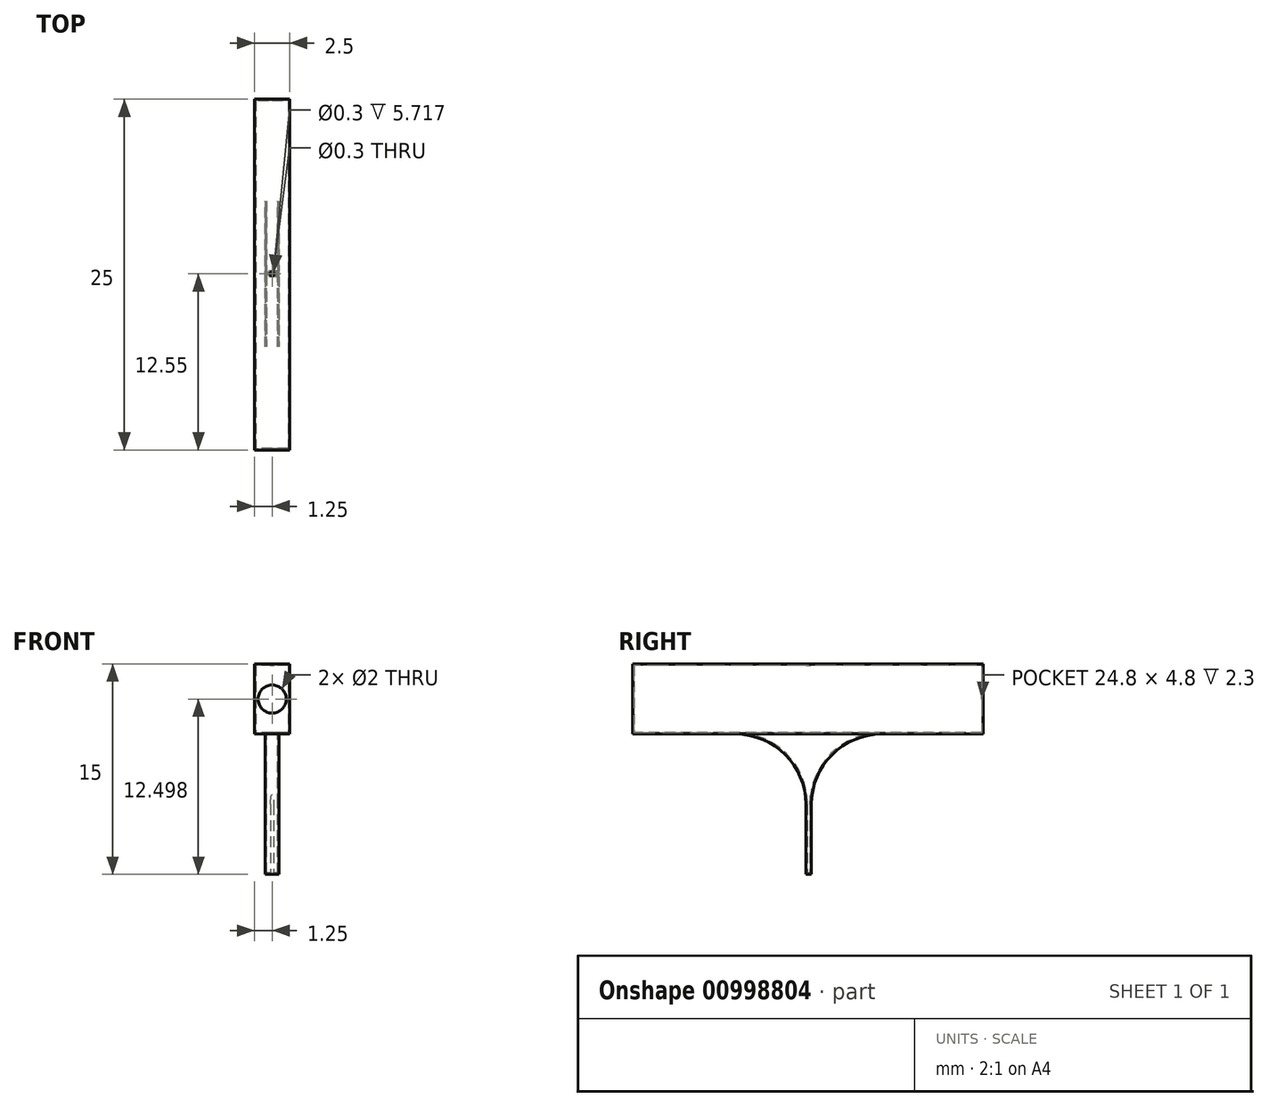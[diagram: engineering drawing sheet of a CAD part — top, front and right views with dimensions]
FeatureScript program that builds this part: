
annotation { "Feature Type Name" : "Feature", "Feature Type Description" : "" }
export const myFeature = defineFeature(function(context is Context, id is Id, definition is map)
    precondition{}
    {
        {
            var Q0;
            Q0=qCreatedBy(makeId("Right.planeOp"),FACE);
            var sketch = newSketch(context, id + "F0", { "sketchPlane" : qUnion([Q0])});
            skLineSegment(sketch, "E0.bottom", {"start": v(-96.83, 24.86) * mm, "end": v(-121.83, 24.86) * mm});
            skLineSegment(sketch, "E0.top", {"start": v(-114.33, 19.86) * mm, "end": v(-121.83, 19.86) * mm});
            skLineSegment(sketch, "E0.left", {"start": v(-96.83, 24.86) * mm, "end": v(-96.83, 19.86) * mm});
            skLineSegment(sketch, "E0.right", {"start": v(-121.83, 24.86) * mm, "end": v(-121.83, 19.86) * mm});
            skLineSegment(sketch, "E1", {"start": v(-96.78, 19.86) * mm, "end": v(-104.23, 19.86) * mm});
            skPoint(sketch, "E2.newPointB", {"position": v(-109.28, 19.86) * mm});
            skLineSegment(sketch, "E2.filletArc", {"start": v(-109.33, 14.86) * mm, "end": v(-109.33, 14.86) * mm});
            skLineSegment(sketch, "E3", {"start": v(-114.33, 19.86) * mm, "end": v(-114.28, 19.86) * mm});
            skLineSegment(sketch, "E4", {"start": v(-109.28, 19.86) * mm, "end": v(-109.28, 9.86) * mm});
            skLineSegment(sketch, "E5", {"start": v(-109.28, 9.86) * mm, "end": v(-109.48, 9.86) * mm});
            skLineSegment(sketch, "E6", {"start": v(-109.48, 9.86) * mm, "end": v(-109.28, 9.86) * mm});
            skLineSegment(sketch, "E7", {"start": v(-109.28, 9.86) * mm, "end": v(-109.08, 9.86) * mm});
            skLineSegment(sketch, "E8", {"start": v(-109.08, 9.86) * mm, "end": v(-109.08, 14.86) * mm});
            skLineSegment(sketch, "E9", {"start": v(-109.48, 9.86) * mm, "end": v(-109.48, 14.86) * mm});
            skLineSegment(sketch, "E10", {"start": v(-114.33, 19.86) * mm, "end": v(-114.48, 19.86) * mm});
            skLineSegment(sketch, "E11", {"start": v(-104.23, 19.86) * mm, "end": v(-104.08, 19.86) * mm});
            skPoint(sketch, "E12.visualSharp", {"position": v(-109.48, 19.86) * mm});
            skArc(sketch, "E12.filletArc", {"start": v(-109.48, 14.86) * mm, "mid": v(-110.94, 18.4) * mm, "end": v(-114.48, 19.86) * mm});
            skPoint(sketch, "E13.visualSharp", {"position": v(-109.08, 19.86) * mm});
            skArc(sketch, "E13.filletArc", {"start": v(-104.08, 19.86) * mm, "mid": v(-107.62, 18.4) * mm, "end": v(-109.08, 14.86) * mm});
            skLineSegment(sketch, "E14", {"start": v(-114.28, 19.86) * mm, "end": v(-104.23, 19.86) * mm});
            skSolve(sketch);
        }
        {
            var Q0;
            Q0=makeQuery(id+"F0.imprint","IMPRINT",FACE,{"disambiguationData":[TD([[makeQuery(id+"F0.imprint","IMPRINT",EDGE,{"derivedFrom":sQuery(id+"F0.wireOp",EDGE,"E0.bottom")}),1.0]])]});
            extrude(context, id + "F1", {"entities" : qUnion([Q0]), "endBound" : BoundingType.SYMMETRIC, "depth" : 2.5 * mm, "offsetDistance" : 25 * mm});
        }
        {
            var Q0;
            {var subQ1=sQuery(id+"F0.wireOp",EDGE,"E4");Q0=makeQuery(id+"F0.imprint","IMPRINT",FACE,{"disambiguationData":[TD([[makeQuery(id+"F0.imprint","IMPRINT",EDGE,{"derivedFrom":subQ1}),1.0]])]});}
            var Q1;
            {var subQ1=sQuery(id+"F0.wireOp",EDGE,"E3");Q1=makeQuery(id+"F0.imprint","IMPRINT",FACE,{"disambiguationData":[TD([[makeQuery(id+"F0.imprint","IMPRINT",EDGE,{"derivedFrom":subQ1}),-1.0]])]});}
            extrude(context, id + "F2", {"entities" : qUnion([Q0, Q1]), "operationType" : NewBodyOperationType.ADD, "depth" : 0.5 * mm, "offsetDistance" : 25 * mm});
        }
        {
            var Q0;
            {var subQ1=sQuery(id+"F0.wireOp",EDGE,"E4");Q0=makeQuery(id+"F0.imprint","IMPRINT",FACE,{"disambiguationData":[TD([[makeQuery(id+"F0.imprint","IMPRINT",EDGE,{"derivedFrom":subQ1}),1.0]])]});}
            var Q1;
            {var subQ1=sQuery(id+"F0.wireOp",EDGE,"E3");Q1=makeQuery(id+"F0.imprint","IMPRINT",FACE,{"disambiguationData":[TD([[makeQuery(id+"F0.imprint","IMPRINT",EDGE,{"derivedFrom":subQ1}),-1.0]])]});}
            extrude(context, id + "F3", {"entities" : qUnion([Q0, Q1]), "operationType" : NewBodyOperationType.ADD, "oppositeDirection" : true, "depth" : 0.5 * mm, "offsetDistance" : 25 * mm});
        }
        {
            var Q0;
            Q0=makeQuery(id+"F1.opExtrude","SWEPT_FACE",FACE,{"disambiguationData":[OSD([sQuery(id+"F0.wireOp",EDGE,"E0.left")])]});
            var Q1;
            Q1=makeQuery(id+"F1.opExtrude","SWEPT_FACE",FACE,{"disambiguationData":[OSD([sQuery(id+"F0.wireOp",EDGE,"E0.right")])]});
            shell(context, id + "F4", {"entities" : qUnion([Q0, Q1]), "thickness" : 0.1 * mm});
        }
        {
            var Q0;
            Q0=makeQuery(id+"F1.opExtrude","SWEPT_FACE",FACE,{"disambiguationData":[OSD([sQuery(id+"F0.wireOp",EDGE,"E0.right")])]});
            var sketch = newSketch(context, id + "F5", { "sketchPlane" : qUnion([Q0])});
            skLineSegment(sketch, "E15.bottom", {"start": v(-1.15, 24.76) * mm, "end": v(1.15, 24.76) * mm});
            skLineSegment(sketch, "E15.top", {"start": v(-1.15, 19.96) * mm, "end": v(1.15, 19.96) * mm});
            skLineSegment(sketch, "E15.left", {"start": v(-1.15, 24.76) * mm, "end": v(-1.15, 19.96) * mm});
            skLineSegment(sketch, "E15.right", {"start": v(1.15, 24.76) * mm, "end": v(1.15, 19.96) * mm});
            skLineSegment(sketch, "E16", {"start": v(0, 24.86) * mm, "end": v(0, 19.96) * mm});
            skLineSegment(sketch, "E17", {"start": v(0, 19.96) * mm, "end": v(0, 22.4) * mm});
            skSolve(sketch);
        }
        {
            var Q0;
            Q0=makeQuery(id+"F5.imprint","IMPRINT",FACE,{"disambiguationData":[TD([[makeQuery(id+"F5.imprint","IMPRINT",EDGE,{"derivedFrom":sQuery(id+"F5.wireOp",EDGE,"E15.bottom")}),1.0]])]});
            extrude(context, id + "F6", {"entities" : qUnion([Q0]), "operationType" : NewBodyOperationType.ADD, "oppositeDirection" : true, "depth" : 0.1 * mm, "offsetDistance" : 25 * mm});
        }
        {
            var Q0;
            Q0=makeQuery(id+"F1.opExtrude","SWEPT_FACE",FACE,{"disambiguationData":[OSD([sQuery(id+"F0.wireOp",EDGE,"E0.left")])]});
            var sketch = newSketch(context, id + "F7", { "sketchPlane" : qUnion([Q0])});
            skLineSegment(sketch, "E18.bottom", {"start": v(-1.15, 24.76) * mm, "end": v(1.15, 24.76) * mm});
            skLineSegment(sketch, "E18.top", {"start": v(-1.15, 19.96) * mm, "end": v(1.15, 19.96) * mm});
            skLineSegment(sketch, "E18.left", {"start": v(-1.15, 24.76) * mm, "end": v(-1.15, 19.96) * mm});
            skLineSegment(sketch, "E18.right", {"start": v(1.15, 24.76) * mm, "end": v(1.15, 19.96) * mm});
            skLineSegment(sketch, "E19", {"start": v(0, 24.76) * mm, "end": v(0, 19.96) * mm});
            skLineSegment(sketch, "E20", {"start": v(0, 19.96) * mm, "end": v(0, 22.36) * mm});
            skSolve(sketch);
        }
        {
            var Q0;
            {var subQ0=sQuery(id+"F7.wireOp",EDGE,"E18.right");var subQ9=sQuery(id+"F7.wireOp",EDGE,"E18.left");Q0=qUnion([makeQuery(id+"F7.imprint","IMPRINT",FACE,{"disambiguationData":[TD([[makeQuery(id+"F7.imprint","IMPRINT",EDGE,{"derivedFrom":subQ9}),1.0]])]}),makeQuery(id+"F7.imprint","IMPRINT",FACE,{"disambiguationData":[TD([[makeQuery(id+"F7.imprint","IMPRINT",EDGE,{"derivedFrom":subQ0}),-1.0]])]})]);}
            extrude(context, id + "F8", {"entities" : qUnion([Q0]), "operationType" : NewBodyOperationType.ADD, "oppositeDirection" : true, "depth" : 0.1 * mm, "offsetDistance" : 25 * mm});
        }
        {
            var Q0;
            Q0=sQuery(id+"F7.wireOp",VERTEX,"E20.end");
            var Q1;
            Q1=makeQuery(id+"F1.opExtrude","SWEPT_BODY",BODY,{"disambiguationData":[OSD([sQuery(id+"F0.wireOp",EDGE,"E0.bottom"),sQuery(id+"F0.wireOp",EDGE,"E0.top"),sQuery(id+"F0.wireOp",EDGE,"E0.left"),sQuery(id+"F0.wireOp",EDGE,"E0.right"),sQuery(id+"F0.wireOp",EDGE,"E1"),sQuery(id+"F0.wireOp",EDGE,"E3"),sQuery(id+"F0.wireOp",EDGE,"E10"),sQuery(id+"F0.wireOp",EDGE,"E11"),sQuery(id+"F0.wireOp",EDGE,"E14")])]});
            hole(context, id + "F9", {"style" : HoleStyle.SIMPLE, "endStyle" : HoleEndStyle.THROUGH, "holeDiameter" : 2 * mm, "majorDiameter" : 5 * mm, "isTappedThrough" : true, "tappedDepth" : 12 * mm, "tapClearance" : 3, "locations" : qUnion([Q0]), "scope" : qUnion([Q1])});
        }
        {
            var Q0;
            {var subQ0=sQuery(id+"F0.wireOp",EDGE,"E7");var subQ1=sQuery(id+"F0.wireOp",EDGE,"E6");Q0=makeQuery(id+"F3.boolean.opBoolean","MERGE",FACE,{"derivedFrom":[makeQuery(id+"F2.opExtrude","SWEPT_FACE",FACE,{"disambiguationData":[OSD([subQ1,subQ0])]}),makeQuery(id+"F3.opExtrude","SWEPT_FACE",FACE,{"disambiguationData":[OSD([subQ1,subQ0])]})]});}
            var sketch = newSketch(context, id + "F10", { "sketchPlane" : qUnion([Q0])});
            skLineSegment(sketch, "E21.bottom", {"start": v(0.5, 109.48) * mm, "end": v(-0.5, 109.48) * mm});
            skLineSegment(sketch, "E21.top", {"start": v(0.5, 109.08) * mm, "end": v(-0.5, 109.08) * mm});
            skLineSegment(sketch, "E21.left", {"start": v(0.5, 109.48) * mm, "end": v(0.5, 109.08) * mm});
            skLineSegment(sketch, "E21.right", {"start": v(-0.5, 109.48) * mm, "end": v(-0.5, 109.08) * mm});
            skLineSegment(sketch, "E22", {"start": v(0, 109.48) * mm, "end": v(0, 109.08) * mm});
            skLineSegment(sketch, "E23", {"start": v(0, 109.08) * mm, "end": v(0, 109.28) * mm});
            skSolve(sketch);
        }
        {
            var Q0;
            Q0=sQuery(id+"F10.wireOp",VERTEX,"E23.end");
            var Q1;
            Q1=makeQuery(id+"F1.opExtrude","SWEPT_BODY",BODY,{"disambiguationData":[OSD([sQuery(id+"F0.wireOp",EDGE,"E0.bottom"),sQuery(id+"F0.wireOp",EDGE,"E0.top"),sQuery(id+"F0.wireOp",EDGE,"E0.left"),sQuery(id+"F0.wireOp",EDGE,"E0.right"),sQuery(id+"F0.wireOp",EDGE,"E1"),sQuery(id+"F0.wireOp",EDGE,"E3"),sQuery(id+"F0.wireOp",EDGE,"E10"),sQuery(id+"F0.wireOp",EDGE,"E11"),sQuery(id+"F0.wireOp",EDGE,"E14")])]});
            hole(context, id + "F11", {"style" : HoleStyle.SIMPLE, "endStyle" : HoleEndStyle.THROUGH, "holeDiameter" : 0.3 * mm, "majorDiameter" : 5 * mm, "isTappedThrough" : true, "tappedDepth" : 12 * mm, "tapClearance" : 3, "locations" : qUnion([Q0]), "scope" : qUnion([Q1])});
        }
    });
